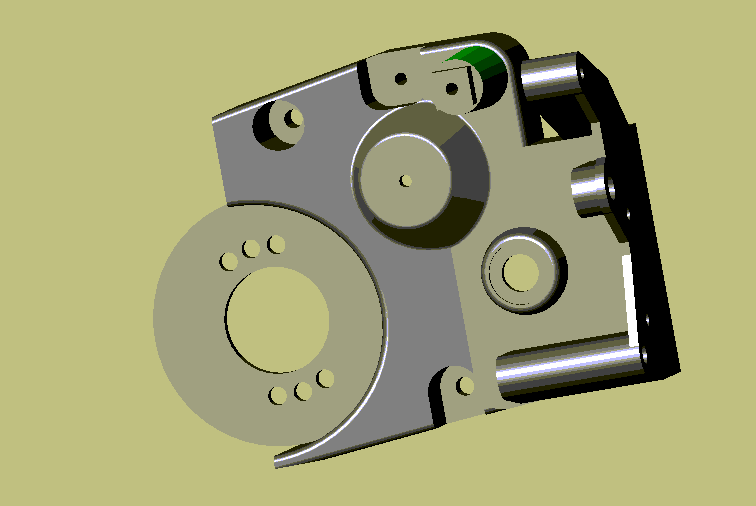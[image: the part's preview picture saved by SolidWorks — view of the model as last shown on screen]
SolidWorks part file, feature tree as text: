
SOLIDWORKS PART (.sldprt)
format: sldprt  version: not decoded by parser v0  size: 799,744 bytes
history: native  units: mm
features: sketch x40, cut_extrude x19, extrude x18, plane x7, fillet x5, material x1, shell x1 (+8 scaffold rows collapsed)
feature tree (99):
  scaffold x8  (default folders/planes/origin — collapsed)
  material  "Matériau <non spécifié>"
  plane  "Plane1"
  plane  "Plane2"
  plane  "Plane3"
  sketch  "Esquisse1"  dims[D1=45.0mm D2=12.0mm D3=22.0mm D4=18.0mm D5=15.0mm D6=40.0mm D7=20.0mm D8=35.0mm]
  sketch  "Esquisse2"  dims[c1.D8=7.0mm c1.D1=18.0mm c1.D2=12.0mm c2.D1=8.0mm c2.D2=4.0mm c2.D3=14.0mm c2.D4=130.0mm c2.D5=22.0mm c2.D6=174.5mm c2.D7=22.0mm]
  sketch  "Esquisse3"  dims[c1.D2=36.0mm c1.D1=34.0mm c1.D5=24.0mm c1.D6=17.0mm c1.D7=12.0mm c1.D10=16.5mm c1.D11=~11.949177mm c2.D1=222.0mm c2.D3=27.0mm c3.D1=217.0mm c3.D3=228.0mm c4.D1=22.8mm c4.D4=19.0mm c5.D1=22.8mm c5.D4=13.0mm c5.D5=14.0mm c5.D6=18.0mm c5.D8=30.0mm c5.D9=2.0mm c5.D2=2.0mm c6.D9=~17.995555mm c6.D6=~17.995555mm c6.D5=19.25mm c7.D6=18.0mm c7.D9=21.0mm]
  sketch  "Esquisse4"  dims[D1=40.0mm D2=7.5mm D3=25.5mm D4=4.7mm]
  extrude  "Base-Extrusion"  Depth=22mm
  sketch  "Esquisse5"  dims[D1=33.0mm D2=13.0mm]
  cut_extrude  "Enlèv. mat.-Extru.1"  [1 undecoded]
  fillet  "Congé1"  Radius=6mm
  fillet  "Congé2"  Radius=6mm
  sketch  "Esquisse6"  dims[D1=40.0mm D2=36.0mm]
  extrude  "Boss.-Extru.1"  Depth=2mm
  sketch  "Esquisse7"  dims[D1=17.0mm]
  cut_extrude  "Enlèv. mat.-Extru.2"  [1 undecoded]
  sketch  "Esquisse9"  dims[D1=25.0mm]
  extrude  "Boss.-Extru.3"  Depth=5mm
  shell  "Coque4"  Thickness=2mm
  sketch  "Esquisse11"  dims[D1=9.0mm D2=~17.252312mm]
  extrude  "Boss.-Extru.4"  Depth=6mm
  sketch  "Esquisse16"  dims[c1.D1=15.0mm c1.D2=23.2mm c1.D3=~38.166952mm c2.D2=23.2mm c2.D3=40.5mm c2.D1=23.2mm c3.D2=15.28mm]
  extrude  "Boss.-Extru.5"  Depth=4mm
  sketch  "Esquisse17"  dims[D1=10.0mm]
  cut_extrude  "Enlèv. mat.-Extru.4"  Depth=0.5mm
  sketch  "Esquisse18"  dims[D1=6.0mm]
  cut_extrude  "Enlèv. mat.-Extru.5"  [1 undecoded]
  sketch  "Esquisse19"  dims[c1.D1=11.0mm c1.D3=11.0mm c2.D1=23.2mm c2.D2=15.28mm]
  cut_extrude  "Enlèv. mat.-Extru.6"  Depth=4mm
  fillet  "Congé3"  Radius=1mm
  sketch  "Esquisse20"  dims[c1.D3=7.0mm c1.D6=9.0mm c1.D9=7.0mm c2.D3=7.0mm c2.D24=3.5mm c2.D25=4.5mm c2.D26=3.5mm c2.D1=21.0mm c2.D2=5.0mm c2.D4=27.0mm c2.D5=23.0mm c2.D7=19.0mm c2.D8=29.0mm c2.D9=29.0mm c2.D10=23.0mm c2.D11=18.0mm c3.D4=~15.138462mm c3.D1=40.0mm c3.D2=~8.609482mm c3.D3=~2.390518mm c4.D4=~3.275048mm c4.D5=~8.138852mm c4.D6=~9.104016mm c4.D7=~6.666751mm c4.D8=~9.133558mm c4.D9=~1.508725mm c4.D10=~14.09962mm c4.D11=2.0mm c4.D12=~5.379326mm c4.D13=~5.570033mm c4.D14=~5.271711mm c4.D15=~10.246973mm c4.D16=~6.064391mm c4.D17=~7.362359mm c4.D18=5.0mm c4.D19=32.0mm c4.D20=51.0mm c4.D21=10.0mm c4.D22=12.0mm c4.D23=18.0mm c4.D26=13.0mm c4.D27=40.0mm]
  extrude  "Boss.-Extru.6"  Depth=1.5mm
  sketch  "Esquisse21"  dims[D1=2.0mm]
  cut_extrude  "Enlèv. mat.-Extru.7"  [1 undecoded]
  sketch  "Esquisse22"
  extrude  "Boss.-Extru.7"  Depth=22mm
  sketch  "Esquisse23"  dims[D1=8.0mm]
  extrude  "Boss.-Extru.8"  Depth=4mm
  sketch  "Esquisse25"  dims[D1=3.5mm D2=~7.602811mm D3=~7.723457mm D4=~19.230556mm D5=~18.93016mm D6=~1.772245mm D7=11.0mm D8=13.0mm D9=40.0mm]
  extrude  "Boss.-Extru.9"  Depth=6mm
  sketch  "Esquisse26"  dims[D4=3.5mm D1=~8.138852mm D2=~19.161831mm D3=~7.698463mm D5=~15.823291mm D6=~9.104016mm D7=~8.609482mm D8=~5.674137mm D9=11.0mm D10=~26.138852mm]
  extrude  "Boss.-Extru.10"  Depth=1.5mm
  sketch  "Esquisse27"  dims[D1=3.0mm D2=4.0mm D3=2.0mm]
  cut_extrude  "Enlèv. mat.-Extru.8"  [1 undecoded]
  fillet  "Congé4"  Radius=1mm
  fillet  "Congé5"  Radius=0.75mm
  sketch  "Esquisse28"  dims[D2=9.0mm D1=16.0mm]
  extrude  "Boss.-Extru.11"  Depth=3mm
  sketch  "Esquisse29"  dims[D1=4.0mm D2=~12.43018mm]
  cut_extrude  "Enlèv. mat.-Extru.9"  Depth=3mm
  sketch  "Esquisse30"  dims[D4=2.0mm D5=2.0mm D1=10.0mm D2=17.0mm D3=16.6mm]
  cut_extrude  "Enlèv. mat.-Extru.10"  Depth=10mm
  sketch  "Esquisse31"  dims[D1=3.0mm D2=3.0mm D3=3.0mm D4=3.0mm D5=3.0mm D6=3.0mm D7=~3.916222mm D8=~4.167556mm D9=12.0mm D10=12.0mm D11=12.0mm D12=~2.083778mm D13=~4.167556mm D14=~3.916222mm D15=~1.425388mm D16=12.0mm D17=12.0mm D18=12.0mm D19=~11.817693mm D20=~11.817693mm]
  cut_extrude  "Enlèv. mat.-Extru.11"  [1 undecoded]
  sketch  "Esquisse32"  dims[D2=10.0mm D1=9.9mm D3=4.91mm]
  extrude  "Boss.-Extru.12"  [1 undecoded]
  plane  "Plan1"  Offset=8mm
  sketch  "Esquisse33"  dims[D1=8.0mm]
  cut_extrude  "Enlèv. mat.-Extru.12"  [1 undecoded]
  sketch  "Esquisse34"  dims[D1=7.0mm]
  cut_extrude  "Enlèv. mat.-Extru.13"  Depth=3mm
  sketch  "Esquisse35"  dims[D1=3.0mm]
  cut_extrude  "Enlèv. mat.-Extru.14"  [1 undecoded]
  sketch  "Esquisse36"  dims[D3=10.0mm D1=6.0mm D2=6.0mm]
  extrude  "Boss.-Extru.13"  Depth=16mm
  sketch  "Esquisse37"  dims[D1=6.0mm D2=6.0mm D3=3.0mm D4=3.0mm]
  extrude  "Boss.-Extru.14"  Depth=3mm
  sketch  "Esquisse38"  dims[D1=2.0mm]
  cut_extrude  "Enlèv. mat.-Extru.15"  Depth=10mm
  sketch  "Esquisse40"  dims[D3=10.0mm D1=33.5mm D2=5.0mm]
  extrude  "Boss.-Extru.15"  [1 undecoded]
  sketch  "Esquisse41"  dims[D1=7.0mm]
  cut_extrude  "Enlèv. mat.-Extru.16"  Depth=3mm
  plane  "Plan2"  Offset=3mm
  sketch  "Esquisse42"  dims[D1=8.0mm]
  cut_extrude  "Enlèv. mat.-Extru.17"  [1 undecoded]
  sketch  "Esquisse43"  dims[D1=3.0mm]
  cut_extrude  "Enlèv. mat.-Extru.18"  [1 undecoded]
  sketch  "Esquisse44"  dims[D2=6.0mm D1=4.5mm]
  extrude  "Boss.-Extru.21"  Depth=5mm
  plane  "Plan3"  Offset=5mm
  sketch  "Esquisse45"  dims[D2=3.0mm D1=6.0mm D3=7.5mm]
  extrude  "Boss.-Extru.22"  [1 undecoded]
  sketch  "Esquisse46"  dims[c1.D3=3.0mm c1.D6=3.0mm c2.D3=3.0mm c2.D1=12.0mm c2.D2=6.0mm c3.D3=~19.825172mm c3.D4=4.5mm c3.D5=4.5mm c3.D7=6.0mm c3.D8=~2.790627mm c3.D9=12.0mm c4.D3=~11.924849mm c4.D9=~7.709373mm]
  extrude  "Boss.-Extru.23"  [1 undecoded]
  plane  "Plan4"  Offset=20mm
  sketch  "Esquisse47"  dims[D3=3.0mm D1=5.0mm D2=4.0mm]
  cut_extrude  "Enlèv. mat.-Extru.19"  Depth=12mm
  sketch  "Esquisse48"  dims[D1=2.0mm]
  cut_extrude  "Enlèv. mat.-Extru.20"  [1 undecoded]
decode coverage: 67 of 83 modeling features carry decoded parameters
note: ~ marks probable driven/reference dimensions
note: 15 parameter values undecoded
summary: no parameter record found for 15 features
note: suppression state not decoded; provenance and decode notes live in map.json
